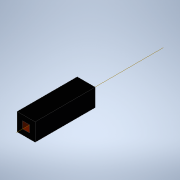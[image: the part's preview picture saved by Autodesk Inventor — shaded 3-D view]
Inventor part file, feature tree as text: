
AUTODESK INVENTOR PART (.ipt)
format: ipt  version: 2020 (Build 240168000, 168)  size: 102,400 bytes
history: native  units: in
note: dims shown in document units (in); Inventor stores cm internally (conversion verified against a paired STEP export)
features: other x2, plane x2
ambient origin geometry x8: Origin, YZ Plane, XZ Plane, XY Plane, X Axis, Y Axis, Z Axis, Center Point
bodies: Solid1 (feature_tree)
feature tree (4):
  other  "Part1"
  other  "Work Axis1"
  plane  "Work Plane1"
  plane  "Work Plane2"
